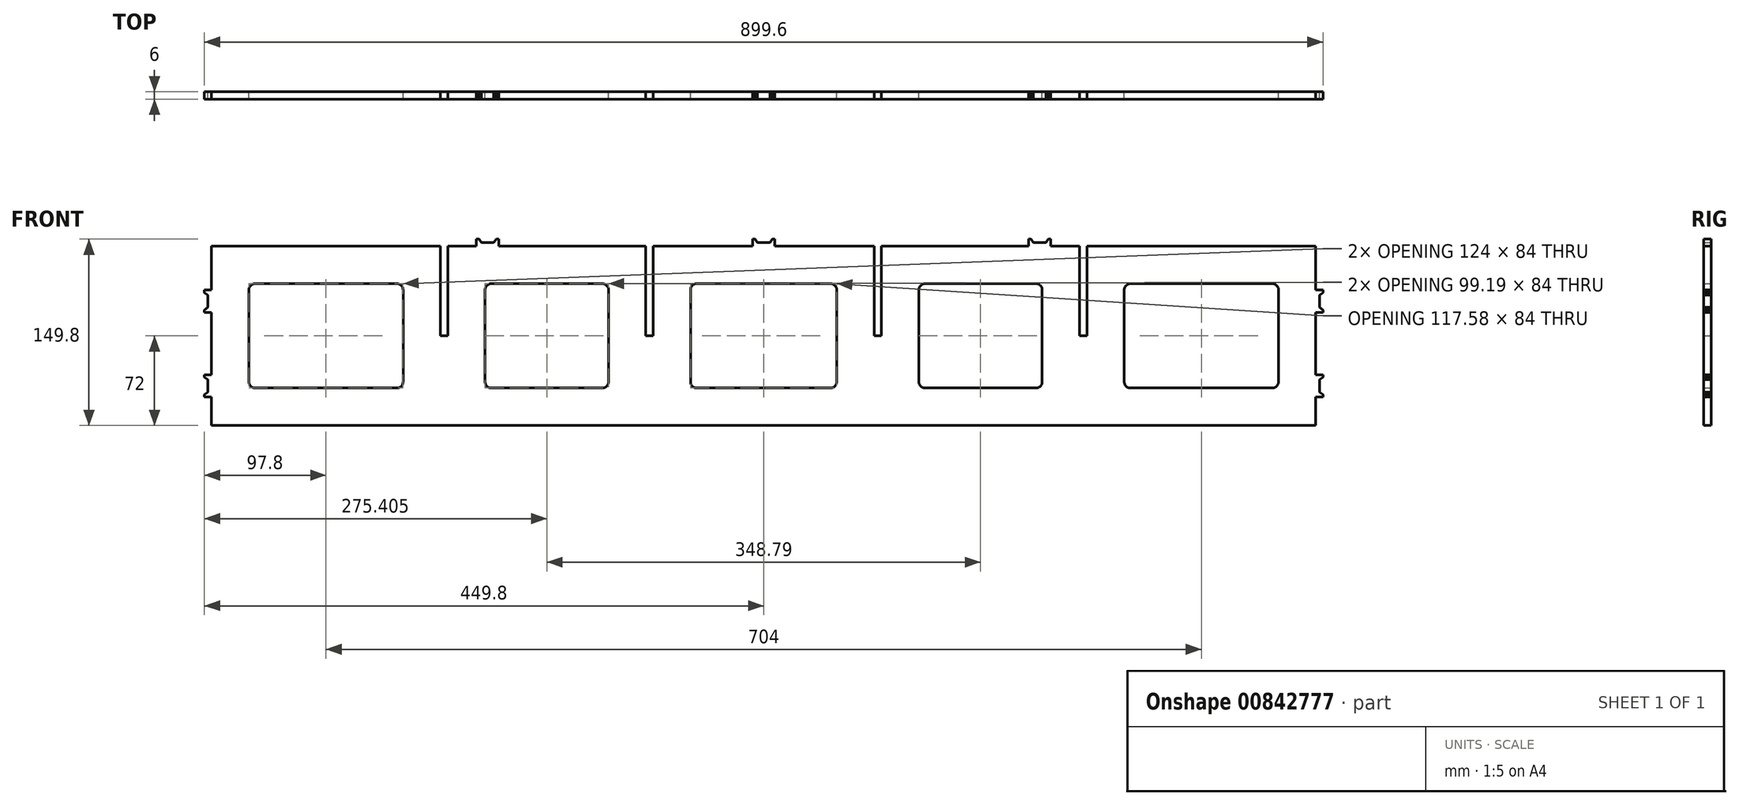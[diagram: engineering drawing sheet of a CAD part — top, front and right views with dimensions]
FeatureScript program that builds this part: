
annotation { "Feature Type Name" : "Feature", "Feature Type Description" : "" }
export const myFeature = defineFeature(function(context is Context, id is Id, definition is map)
    precondition{}
    {
        {
            var Q0;
            Q0=qCreatedBy(makeId("Front.planeOp"),FACE);
            var sketch = newSketch(context, id + "F0", { "sketchPlane" : qUnion([Q0])});
            skLineSegment(sketch, "E0.bottom", {"start": v(0, 0) * mm, "end": v(184, 0) * mm});
            skLineSegment(sketch, "E0.top", {"start": v(0, -144) * mm, "end": v(888, -144) * mm});
            skLineSegment(sketch, "E0.left", {"start": v(0, 0) * mm, "end": v(0, -35.2) * mm});
            skLineSegment(sketch, "E0.right", {"start": v(888, 0) * mm, "end": v(888, -35.2) * mm});
            skLineSegment(sketch, "E1", {"start": v(213, 0) * mm, "end": v(213, 5.8) * mm});
            skLineSegment(sketch, "E2", {"start": v(213, 5.8) * mm, "end": v(215, 5.8) * mm});
            skLineSegment(sketch, "E3", {"start": v(215, 5.8) * mm, "end": v(217, 3) * mm});
            skLineSegment(sketch, "E4", {"start": v(217, 3) * mm, "end": v(227, 3) * mm});
            skLineSegment(sketch, "E5", {"start": v(227, 3) * mm, "end": v(229, 5.8) * mm});
            skLineSegment(sketch, "E6", {"start": v(229, 5.8) * mm, "end": v(231, 5.8) * mm});
            skLineSegment(sketch, "E7", {"start": v(231, 5.8) * mm, "end": v(231, 0) * mm});
            skLineSegment(sketch, "E8.trimOffspring", {"start": v(231, 0) * mm, "end": v(349.2, 0) * mm});
            skLineSegment(sketch, "E9", {"start": v(435, 0) * mm, "end": v(435, 5.8) * mm});
            skLineSegment(sketch, "E10", {"start": v(435, 5.8) * mm, "end": v(437, 5.8) * mm});
            skLineSegment(sketch, "E11", {"start": v(437, 5.8) * mm, "end": v(439, 3) * mm});
            skLineSegment(sketch, "E12", {"start": v(439, 3) * mm, "end": v(449, 3) * mm});
            skLineSegment(sketch, "E13", {"start": v(449, 3) * mm, "end": v(451, 5.8) * mm});
            skLineSegment(sketch, "E14", {"start": v(451, 5.8) * mm, "end": v(453, 5.8) * mm});
            skLineSegment(sketch, "E15", {"start": v(453, 5.8) * mm, "end": v(453, 0) * mm});
            skLineSegment(sketch, "E16.trimOffspring", {"start": v(453, 0) * mm, "end": v(532.8, 0) * mm});
            skLineSegment(sketch, "E17", {"start": v(657, 0) * mm, "end": v(657, 5.8) * mm});
            skLineSegment(sketch, "E18", {"start": v(657, 5.8) * mm, "end": v(659, 5.8) * mm});
            skLineSegment(sketch, "E19", {"start": v(659, 5.8) * mm, "end": v(661, 3) * mm});
            skLineSegment(sketch, "E20", {"start": v(661, 3) * mm, "end": v(671, 3) * mm});
            skLineSegment(sketch, "E21", {"start": v(671, 3) * mm, "end": v(673, 5.8) * mm});
            skLineSegment(sketch, "E22", {"start": v(673, 5.8) * mm, "end": v(675, 5.8) * mm});
            skLineSegment(sketch, "E23", {"start": v(675, 5.8) * mm, "end": v(675, 0) * mm});
            skLineSegment(sketch, "E24", {"start": v(0, -35.2) * mm, "end": v(-5.8, -35.2) * mm});
            skLineSegment(sketch, "E25", {"start": v(-5.8, -35.2) * mm, "end": v(-5.8, -37.2) * mm});
            skLineSegment(sketch, "E26", {"start": v(-5.8, -37.2) * mm, "end": v(-3, -39.2) * mm});
            skLineSegment(sketch, "E27", {"start": v(-3, -39.2) * mm, "end": v(-3, -49.2) * mm});
            skLineSegment(sketch, "E28", {"start": v(-3, -49.2) * mm, "end": v(-5.8, -51.21) * mm});
            skLineSegment(sketch, "E29", {"start": v(-5.8, -51.21) * mm, "end": v(-5.8, -53.21) * mm});
            skLineSegment(sketch, "E30", {"start": v(-5.8, -53.21) * mm, "end": v(0, -53.21) * mm});
            skLineSegment(sketch, "E31", {"start": v(0, -103.23) * mm, "end": v(-5.8, -103.23) * mm});
            skLineSegment(sketch, "E32", {"start": v(-5.8, -103.23) * mm, "end": v(-5.8, -105.23) * mm});
            skLineSegment(sketch, "E33", {"start": v(-5.8, -105.23) * mm, "end": v(-3, -107.23) * mm});
            skLineSegment(sketch, "E34", {"start": v(-3, -107.23) * mm, "end": v(-3, -117.23) * mm});
            skLineSegment(sketch, "E35", {"start": v(-3, -117.23) * mm, "end": v(-5.8, -119.23) * mm});
            skLineSegment(sketch, "E36", {"start": v(-5.8, -119.23) * mm, "end": v(-5.8, -121.23) * mm});
            skLineSegment(sketch, "E37", {"start": v(-5.8, -121.23) * mm, "end": v(0, -121.23) * mm});
            skLineSegment(sketch, "E38.trimOffspring", {"start": v(0, -53.21) * mm, "end": v(0, -103.23) * mm});
            skLineSegment(sketch, "E39", {"start": v(888, -35.2) * mm, "end": v(893.8, -35.2) * mm});
            skLineSegment(sketch, "E40", {"start": v(893.8, -35.2) * mm, "end": v(893.8, -37.2) * mm});
            skLineSegment(sketch, "E41", {"start": v(893.8, -37.2) * mm, "end": v(891, -39.2) * mm});
            skLineSegment(sketch, "E42", {"start": v(891, -39.2) * mm, "end": v(891, -49.2) * mm});
            skLineSegment(sketch, "E43", {"start": v(891, -49.21) * mm, "end": v(893.8, -51.21) * mm});
            skLineSegment(sketch, "E44", {"start": v(893.8, -51.2) * mm, "end": v(893.8, -53.2) * mm});
            skLineSegment(sketch, "E45", {"start": v(893.8, -53.2) * mm, "end": v(888, -53.2) * mm});
            skLineSegment(sketch, "E46.trimOffspring", {"start": v(888, -53.2) * mm, "end": v(888, -103.23) * mm});
            skLineSegment(sketch, "E47", {"start": v(888, -103.23) * mm, "end": v(893.8, -103.23) * mm});
            skLineSegment(sketch, "E48", {"start": v(893.8, -103.23) * mm, "end": v(893.8, -105.23) * mm});
            skLineSegment(sketch, "E49", {"start": v(893.8, -105.23) * mm, "end": v(891, -107.23) * mm});
            skLineSegment(sketch, "E50", {"start": v(891, -107.23) * mm, "end": v(891, -117.23) * mm});
            skLineSegment(sketch, "E51", {"start": v(891, -117.23) * mm, "end": v(893.8, -119.23) * mm});
            skLineSegment(sketch, "E52", {"start": v(893.8, -119.23) * mm, "end": v(893.8, -121.23) * mm});
            skLineSegment(sketch, "E53", {"start": v(893.8, -121.23) * mm, "end": v(888, -121.23) * mm});
            skLineSegment(sketch, "E54", {"start": v(675, 0) * mm, "end": v(697.99, 0) * mm});
            skLineSegment(sketch, "E55", {"start": v(184, 0) * mm, "end": v(184, -72.01) * mm});
            skLineSegment(sketch, "E56", {"start": v(184, -72.01) * mm, "end": v(190, -72.01) * mm});
            skLineSegment(sketch, "E57", {"start": v(190, -72.01) * mm, "end": v(190, 0) * mm});
            skLineSegment(sketch, "E58.trimOffspring", {"start": v(190, 0) * mm, "end": v(213, 0) * mm});
            skLineSegment(sketch, "E59", {"start": v(349.2, 0) * mm, "end": v(349.2, -72) * mm});
            skLineSegment(sketch, "E60", {"start": v(349.2, -72) * mm, "end": v(355.2, -72) * mm});
            skLineSegment(sketch, "E61", {"start": v(355.2, -72) * mm, "end": v(355.2, 0) * mm});
            skLineSegment(sketch, "E62.trimOffspring", {"start": v(355.2, 0) * mm, "end": v(435, 0) * mm});
            skLineSegment(sketch, "E63", {"start": v(532.8, 0) * mm, "end": v(532.8, -72) * mm});
            skLineSegment(sketch, "E64", {"start": v(532.8, -72) * mm, "end": v(538.8, -72) * mm});
            skLineSegment(sketch, "E65", {"start": v(538.8, -72) * mm, "end": v(538.8, 0) * mm});
            skLineSegment(sketch, "E66.trimOffspring", {"start": v(538.8, 0) * mm, "end": v(657, 0) * mm});
            skLineSegment(sketch, "E67", {"start": v(697.99, 0) * mm, "end": v(697.99, -72) * mm});
            skLineSegment(sketch, "E68", {"start": v(697.99, -72) * mm, "end": v(704, -72) * mm});
            skLineSegment(sketch, "E69", {"start": v(704, -72) * mm, "end": v(704, 0) * mm});
            skLineSegment(sketch, "E70.trimOffspring", {"start": v(704, 0) * mm, "end": v(888, 0) * mm});
            skLineSegment(sketch, "E71.trimOffspring", {"start": v(0, -121.23) * mm, "end": v(0, -144) * mm});
            skLineSegment(sketch, "E72.trimOffspring", {"start": v(888, -121.23) * mm, "end": v(888, -144) * mm});
            skLineSegment(sketch, "E73", {"start": v(35, -30) * mm, "end": v(149, -30) * mm});
            skLineSegment(sketch, "E74", {"start": v(154, -35) * mm, "end": v(154, -109) * mm});
            skLineSegment(sketch, "E75", {"start": v(149, -114) * mm, "end": v(35, -114) * mm});
            skLineSegment(sketch, "E76", {"start": v(30, -109) * mm, "end": v(30, -35) * mm});
            skLineSegment(sketch, "E77", {"start": v(220, -35) * mm, "end": v(220, -109) * mm});
            skPoint(sketch, "E77.startSnap0", {"position": v(92, -30) * mm});
            skLineSegment(sketch, "E78", {"start": v(225, -114) * mm, "end": v(314.2, -114) * mm});
            skLineSegment(sketch, "E79", {"start": v(319.2, -109) * mm, "end": v(319.2, -35) * mm});
            skLineSegment(sketch, "E80", {"start": v(314.2, -30) * mm, "end": v(225, -30) * mm});
            skLineSegment(sketch, "E81", {"start": v(390.2, -30) * mm, "end": v(497.79, -30) * mm});
            skPoint(sketch, "E81.startSnap0", {"position": v(269.6, -30) * mm});
            skLineSegment(sketch, "E82", {"start": v(502.79, -35) * mm, "end": v(502.79, -109) * mm});
            skLineSegment(sketch, "E83", {"start": v(497.79, -114) * mm, "end": v(390.2, -114) * mm});
            skLineSegment(sketch, "E84", {"start": v(385.2, -109) * mm, "end": v(385.2, -35) * mm});
            skLineSegment(sketch, "E85", {"start": v(573.8, -30) * mm, "end": v(662.99, -30) * mm});
            skLineSegment(sketch, "E86", {"start": v(667.99, -35) * mm, "end": v(667.99, -109) * mm});
            skLineSegment(sketch, "E87", {"start": v(662.99, -114) * mm, "end": v(573.8, -114) * mm});
            skLineSegment(sketch, "E88", {"start": v(568.8, -109) * mm, "end": v(568.8, -35) * mm});
            skLineSegment(sketch, "E89", {"start": v(739, -30) * mm, "end": v(853, -30) * mm});
            skLineSegment(sketch, "E90", {"start": v(858, -35) * mm, "end": v(858, -109) * mm});
            skLineSegment(sketch, "E91", {"start": v(853, -114) * mm, "end": v(739, -114) * mm});
            skLineSegment(sketch, "E92", {"start": v(734, -109) * mm, "end": v(734, -35) * mm});
            skPoint(sketch, "E93.visualSharp", {"position": v(30, -30) * mm});
            skArc(sketch, "E93.filletArc", {"start": v(35, -30) * mm, "mid": v(31.46, -31.46) * mm, "end": v(30, -35) * mm});
            skPoint(sketch, "E94.visualSharp", {"position": v(154, -30) * mm});
            skArc(sketch, "E94.filletArc", {"start": v(154, -35) * mm, "mid": v(152.54, -31.46) * mm, "end": v(149, -30) * mm});
            skPoint(sketch, "E95.visualSharp", {"position": v(154, -114) * mm});
            skArc(sketch, "E95.filletArc", {"start": v(149, -114) * mm, "mid": v(152.54, -112.54) * mm, "end": v(154, -109) * mm});
            skPoint(sketch, "E96.visualSharp", {"position": v(30, -114) * mm});
            skArc(sketch, "E96.filletArc", {"start": v(30, -109) * mm, "mid": v(31.46, -112.54) * mm, "end": v(35, -114) * mm});
            skPoint(sketch, "E97.visualSharp", {"position": v(220, -30) * mm});
            skArc(sketch, "E97.filletArc", {"start": v(225, -30) * mm, "mid": v(221.47, -31.46) * mm, "end": v(220, -35) * mm});
            skPoint(sketch, "E98.visualSharp", {"position": v(319.2, -30) * mm});
            skArc(sketch, "E98.filletArc", {"start": v(319.2, -35) * mm, "mid": v(317.74, -31.46) * mm, "end": v(314.2, -30) * mm});
            skPoint(sketch, "E99.visualSharp", {"position": v(319.2, -114) * mm});
            skArc(sketch, "E99.filletArc", {"start": v(314.2, -114) * mm, "mid": v(317.74, -112.54) * mm, "end": v(319.2, -109) * mm});
            skPoint(sketch, "E100.visualSharp", {"position": v(220, -114) * mm});
            skArc(sketch, "E100.filletArc", {"start": v(220, -109) * mm, "mid": v(221.47, -112.54) * mm, "end": v(225, -114) * mm});
            skPoint(sketch, "E101.visualSharp", {"position": v(385.2, -114) * mm});
            skArc(sketch, "E101.filletArc", {"start": v(385.2, -109) * mm, "mid": v(386.67, -112.54) * mm, "end": v(390.2, -114) * mm});
            skPoint(sketch, "E102.visualSharp", {"position": v(385.2, -30) * mm});
            skArc(sketch, "E102.filletArc", {"start": v(390.2, -30) * mm, "mid": v(386.67, -31.46) * mm, "end": v(385.2, -35) * mm});
            skPoint(sketch, "E103.visualSharp", {"position": v(502.79, -30) * mm});
            skArc(sketch, "E103.filletArc", {"start": v(502.79, -35) * mm, "mid": v(501.33, -31.46) * mm, "end": v(497.79, -30) * mm});
            skPoint(sketch, "E104.visualSharp", {"position": v(502.79, -114) * mm});
            skArc(sketch, "E104.filletArc", {"start": v(497.79, -114) * mm, "mid": v(501.33, -112.54) * mm, "end": v(502.79, -109) * mm});
            skPoint(sketch, "E105.visualSharp", {"position": v(568.8, -114) * mm});
            skArc(sketch, "E105.filletArc", {"start": v(568.8, -109) * mm, "mid": v(570.26, -112.54) * mm, "end": v(573.8, -114) * mm});
            skPoint(sketch, "E106.visualSharp", {"position": v(568.8, -30) * mm});
            skArc(sketch, "E106.filletArc", {"start": v(573.8, -30) * mm, "mid": v(570.26, -31.46) * mm, "end": v(568.8, -35) * mm});
            skPoint(sketch, "E107.visualSharp", {"position": v(667.99, -30) * mm});
            skArc(sketch, "E107.filletArc", {"start": v(667.99, -35) * mm, "mid": v(666.53, -31.46) * mm, "end": v(662.99, -30) * mm});
            skPoint(sketch, "E108.visualSharp", {"position": v(667.99, -114) * mm});
            skArc(sketch, "E108.filletArc", {"start": v(662.99, -114) * mm, "mid": v(666.53, -112.54) * mm, "end": v(667.99, -109) * mm});
            skPoint(sketch, "E109.visualSharp", {"position": v(734, -114) * mm});
            skArc(sketch, "E109.filletArc", {"start": v(734, -109) * mm, "mid": v(735.46, -112.54) * mm, "end": v(739, -114) * mm});
            skPoint(sketch, "E110.visualSharp", {"position": v(734, -30) * mm});
            skArc(sketch, "E110.filletArc", {"start": v(739, -30) * mm, "mid": v(735.46, -31.46) * mm, "end": v(734, -35) * mm});
            skPoint(sketch, "E111.visualSharp", {"position": v(858, -30) * mm});
            skArc(sketch, "E111.filletArc", {"start": v(858, -35) * mm, "mid": v(856.54, -31.46) * mm, "end": v(853, -30) * mm});
            skPoint(sketch, "E112.visualSharp", {"position": v(858, -114) * mm});
            skArc(sketch, "E112.filletArc", {"start": v(853, -114) * mm, "mid": v(856.54, -112.54) * mm, "end": v(858, -109) * mm});
            skSolve(sketch);
        }
        {
            var Q0;
            Q0=makeQuery(id+"F0.imprint","IMPRINT",FACE,{"disambiguationData":[TD([[makeQuery(id+"F0.imprint","IMPRINT",EDGE,{"derivedFrom":sQuery(id+"F0.wireOp",EDGE,"E0.bottom")}),-1.0]])]});
            extrude(context, id + "F1", {"entities" : qUnion([Q0]), "depth" : 6 * mm, "offsetDistance" : 25 * mm});
        }
    });
